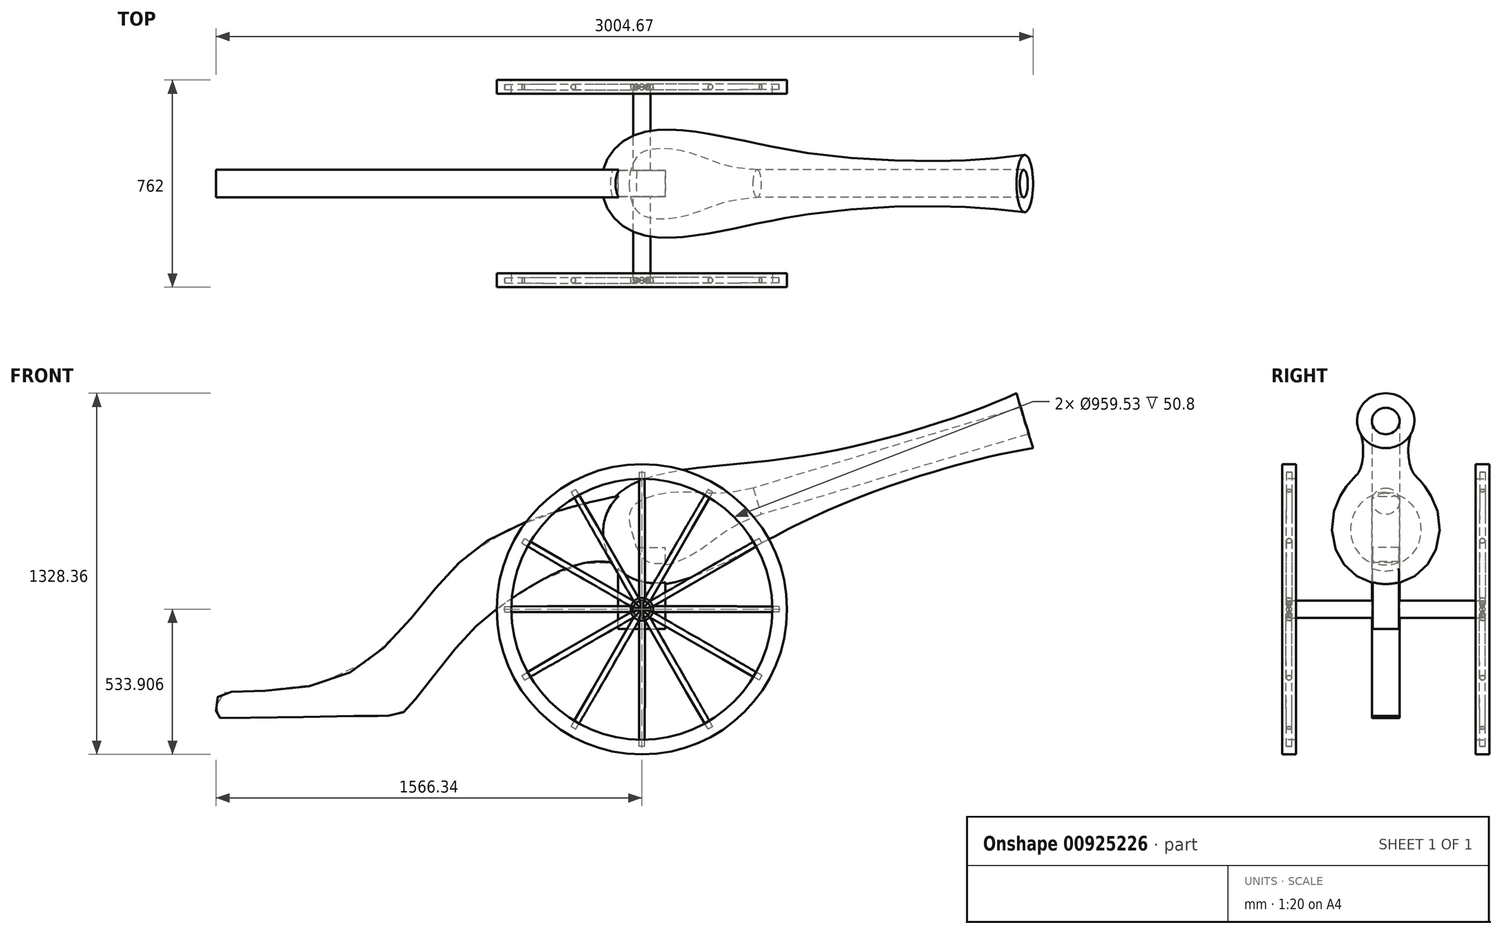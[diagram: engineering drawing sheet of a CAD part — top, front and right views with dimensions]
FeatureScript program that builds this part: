
annotation { "Feature Type Name" : "Feature", "Feature Type Description" : "" }
export const myFeature = defineFeature(function(context is Context, id is Id, definition is map)
    precondition{}
    {
        {
            var Q0;
            Q0=qCreatedBy(makeId("Front.planeOp"),FACE);
            var sketch = newSketch(context, id + "F0", { "sketchPlane" : qUnion([Q0])});
            skLineSegment(sketch, "E0", {"start": v(0, 0) * mm, "end": v(109.65, 33) * mm});
            skFitSpline(sketch, "E1", {"points": [v(0, 0) * mm, v(72.99, 213.2) * mm, v(629.9, 321.57) * mm, v(1200.16, 448.3) * mm, v(1516.96, 566.68) * mm], "startDerivative": vector(-414.8, 1258.42) * mm, "endDerivative": vector(1249.5, 571.91) * mm});
            skLineSegment(sketch, "E2", {"start": v(1516.96, 566.68) * mm, "end": v(1528.95, 513.26) * mm});
            skLineSegment(sketch, "E3", {"start": v(1528.95, 513.26) * mm, "end": v(548.63, 218.19) * mm});
            skFitSpline(sketch, "E4", {"points": [v(548.63, 218.19) * mm, v(418.02, 198.46) * mm, v(244.4, 200.95) * mm, v(100.74, 141) * mm, v(109.65, 33) * mm], "startDerivative": vector(-524.4, -115.88) * mm, "endDerivative": vector(178.23, -541.47) * mm});
            skSolve(sketch);
        }
        {
            var Q0;
            Q0 = qSketchRegion(id + "F0", true);
            var Q1;
            Q1=sQuery(id+"F0.wireOp",EDGE,"E0");
            revolve(context, id + "F1", {"surfaceOperationType" : NewSurfaceOperationType.NEW, "entities" : qUnion([Q0]), "axis" : qUnion([Q1]), "revolveType" : RevolveType.FULL});
        }
        {
            var Q0;
            Q0=qCreatedBy(makeId("Top.planeOp"),FACE);
            var sketch = newSketch(context, id + "F2", { "sketchPlane" : qUnion([Q0])});
            skLineSegment(sketch, "E5.bottom", {"start": v(51.83, 48.12) * mm, "end": v(225.99, 48.12) * mm});
            skLineSegment(sketch, "E5.top", {"start": v(51.83, -48.12) * mm, "end": v(225.99, -48.12) * mm});
            skLineSegment(sketch, "E5.left", {"start": v(51.83, 48.12) * mm, "end": v(51.83, -48.12) * mm});
            skLineSegment(sketch, "E5.right", {"start": v(225.99, 48.12) * mm, "end": v(225.99, -48.12) * mm});
            skPoint(sketch, "E5.middle", {"position": v(138.9, 0) * mm});
            skSolve(sketch);
        }
        {
            var Q0;
            Q0 = qSketchRegion(id + "F2", true);
            extrude(context, id + "F3", {"entities" : qUnion([Q0]), "operationType" : NewBodyOperationType.ADD, "oppositeDirection" : true, "depth" : 299.72 * mm, "offsetDistance" : 25.4 * mm});
        }
        {
            var Q0;
            Q0=qCreatedBy(makeId("Front.planeOp"),FACE);
            var sketch = newSketch(context, id + "F4", { "sketchPlane" : qUnion([Q0])});
            skFitSpline(sketch, "E6", {"points": [v(98.81, 191.9) * mm, v(-314.4, 82.48) * mm, v(-634.52, -169.04) * mm, v(-995.47, -487.53) * mm, v(-1402.16, -536.53) * mm, v(-1423.39, -561.03) * mm, v(-1425.02, -619.82) * mm, v(-1393.99, -627.99) * mm, v(-840.31, -619.82) * mm, v(-825.61, -619.82) * mm, v(-757.02, -614.92) * mm, v(-708.02, -577.36) * mm, v(-521.83, -343.8) * mm, v(-345.44, -191.9) * mm, v(-53.08, -54.71) * mm, v(59.61, -53.08) * mm, v(59.61, -36.75) * mm, v(30.22, 28.58) * mm, v(59.61, 157.6) * mm, v(98.81, 191.9) * mm]});
            skSolve(sketch);
        }
        {
            var Q0;
            Q0 = qSketchRegion(id + "F4", true);
            extrude(context, id + "F5", {"entities" : qUnion([Q0]), "operationType" : NewBodyOperationType.ADD, "depth" : 50.8 * mm, "offsetDistance" : 25.4 * mm, "hasSecondDirection" : true, "secondDirectionOppositeDirection" : true, "secondDirectionDepth" : 50.8 * mm});
        }
        {
            var Q0;
            Q0=qCreatedBy(makeId("Front.planeOp"),FACE);
            var sketch = newSketch(context, id + "F6", { "sketchPlane" : qUnion([Q0])});
            skLineSegment(sketch, "E7", {"start": v(139.4, -303.65) * mm, "end": v(139.4, -227.77) * mm});
            skCircle(sketch, "E8", {"center": v(139.4, -227.77) * mm, "radius": 31.75 * mm});
            skSolve(sketch);
        }
        {
            var Q0;
            Q0 = qSketchRegion(id + "F6", true);
            extrude(context, id + "F7", {"entities" : qUnion([Q0]), "operationType" : NewBodyOperationType.ADD, "depth" : 355.6 * mm, "offsetDistance" : 25.4 * mm, "hasSecondDirection" : true, "secondDirectionOppositeDirection" : true, "secondDirectionDepth" : 355.6 * mm});
        }
        {
            var Q0;
            Q0=makeQuery(id+"F7.opExtrude","CAP_FACE",FACE,{"disambiguationData":[OSD([sQuery(id+"F6.wireOp",EDGE,"E8")])],"isStart":false});
            var sketch = newSketch(context, id + "F8", { "sketchPlane" : qUnion([Q0])});
            skCircle(sketch, "E9", {"center": v(139.4, -227.77) * mm, "radius": 533.9 * mm});
            skCircle(sketch, "E10", {"center": v(139.4, -227.77) * mm, "radius": 479.77 * mm});
            skSolve(sketch);
        }
        {
            var Q0;
            Q0 = qSketchRegion(id + "F8", true);
            extrude(context, id + "F9", {"entities" : qUnion([Q0]), "oppositeDirection" : true, "depth" : 25.4 * mm, "offsetDistance" : 25.4 * mm, "hasSecondDirection" : true, "secondDirectionOppositeDirection" : false, "secondDirectionDepth" : 25.4 * mm});
        }
        {
            var Q0;
            Q0=makeQuery(id+"F7.opExtrude","CAP_FACE",FACE,{"disambiguationData":[OSD([sQuery(id+"F6.wireOp",EDGE,"E8")])],"isStart":false});
            var sketch = newSketch(context, id + "F10", { "sketchPlane" : qUnion([Q0])});
            skLineSegment(sketch, "E11", {"start": v(139.4, -227.77) * mm, "end": v(139.4, -731.61) * mm});
            skLineSegment(sketch, "E12", {"start": v(139.4, -731.61) * mm, "end": v(149.15, -731.61) * mm});
            skLineSegment(sketch, "E13", {"start": v(149.15, -731.61) * mm, "end": v(150.2, -575.12) * mm});
            skLineSegment(sketch, "E14", {"start": v(150.2, -575.12) * mm, "end": v(150.2, -269.13) * mm});
            skLineSegment(sketch, "E15", {"start": v(150.2, -269.13) * mm, "end": v(139.4, -227.77) * mm});
            skSolve(sketch);
        }
        {
            var Q0;
            Q0 = qSketchRegion(id + "F10", true);
            var Q1;
            Q1=sQuery(id+"F10.wireOp",EDGE,"E11");
            revolve(context, id + "F11", {"surfaceOperationType" : NewSurfaceOperationType.NEW, "entities" : qUnion([Q0]), "axis" : qUnion([Q1]), "revolveType" : RevolveType.FULL});
        }
        {
            var Q0;
            Q0=makeQuery(id+"F11.opRevolve","SWEPT_BODY",BODY,{"disambiguationData":[OSD([sQuery(id+"F10.wireOp",EDGE,"E11"),sQuery(id+"F10.wireOp",EDGE,"E12"),sQuery(id+"F10.wireOp",EDGE,"E13"),sQuery(id+"F10.wireOp",EDGE,"E14"),sQuery(id+"F10.wireOp",EDGE,"E15")])]});
            var Q1;
            Q1=makeQuery(id+"F7.opExtrude","CAP_EDGE",EDGE,{"disambiguationData":[OSD([sQuery(id+"F6.wireOp",EDGE,"E8")])],"isStart":false});
            circularPattern(context, id + "F12", {"entities" : qUnion([Q0]), "axis" : qUnion([Q1]), "angle" : 360 * degree, "instanceCount" : 12, "equalSpace" : true});
        }
        {
            var Q0;
            Q0=makeQuery(id+"F9.opExtrude","SWEPT_BODY",BODY,{"disambiguationData":[OSD([sQuery(id+"F8.wireOp",EDGE,"E9"),sQuery(id+"F8.wireOp",EDGE,"E10")])]});
            var Q1;
            Q1=makeQuery(id+"F12.opPattern","COPY",BODY,{"derivedFrom":makeQuery(id+"F11.opRevolve","SWEPT_BODY",BODY,{"disambiguationData":[OSD([sQuery(id+"F10.wireOp",EDGE,"E11"),sQuery(id+"F10.wireOp",EDGE,"E12"),sQuery(id+"F10.wireOp",EDGE,"E13"),sQuery(id+"F10.wireOp",EDGE,"E14"),sQuery(id+"F10.wireOp",EDGE,"E15")])]}),"instanceName":"4"});
            var Q2;
            Q2=makeQuery(id+"F12.opPattern","COPY",BODY,{"derivedFrom":makeQuery(id+"F11.opRevolve","SWEPT_BODY",BODY,{"disambiguationData":[OSD([sQuery(id+"F10.wireOp",EDGE,"E11"),sQuery(id+"F10.wireOp",EDGE,"E12"),sQuery(id+"F10.wireOp",EDGE,"E13"),sQuery(id+"F10.wireOp",EDGE,"E14"),sQuery(id+"F10.wireOp",EDGE,"E15")])]}),"instanceName":"3"});
            var Q3;
            Q3=makeQuery(id+"F12.opPattern","COPY",BODY,{"derivedFrom":makeQuery(id+"F11.opRevolve","SWEPT_BODY",BODY,{"disambiguationData":[OSD([sQuery(id+"F10.wireOp",EDGE,"E11"),sQuery(id+"F10.wireOp",EDGE,"E12"),sQuery(id+"F10.wireOp",EDGE,"E13"),sQuery(id+"F10.wireOp",EDGE,"E14"),sQuery(id+"F10.wireOp",EDGE,"E15")])]}),"instanceName":"2"});
            var Q4;
            Q4=makeQuery(id+"F12.opPattern","COPY",BODY,{"derivedFrom":makeQuery(id+"F11.opRevolve","SWEPT_BODY",BODY,{"disambiguationData":[OSD([sQuery(id+"F10.wireOp",EDGE,"E11"),sQuery(id+"F10.wireOp",EDGE,"E12"),sQuery(id+"F10.wireOp",EDGE,"E13"),sQuery(id+"F10.wireOp",EDGE,"E14"),sQuery(id+"F10.wireOp",EDGE,"E15")])]}),"instanceName":"1"});
            var Q5;
            Q5=makeQuery(id+"F11.opRevolve","SWEPT_BODY",BODY,{"disambiguationData":[OSD([sQuery(id+"F10.wireOp",EDGE,"E11"),sQuery(id+"F10.wireOp",EDGE,"E12"),sQuery(id+"F10.wireOp",EDGE,"E13"),sQuery(id+"F10.wireOp",EDGE,"E14"),sQuery(id+"F10.wireOp",EDGE,"E15")])]});
            var Q6;
            Q6=makeQuery(id+"F12.opPattern","COPY",BODY,{"derivedFrom":makeQuery(id+"F11.opRevolve","SWEPT_BODY",BODY,{"disambiguationData":[OSD([sQuery(id+"F10.wireOp",EDGE,"E11"),sQuery(id+"F10.wireOp",EDGE,"E12"),sQuery(id+"F10.wireOp",EDGE,"E13"),sQuery(id+"F10.wireOp",EDGE,"E14"),sQuery(id+"F10.wireOp",EDGE,"E15")])]}),"instanceName":"11"});
            var Q7;
            Q7=makeQuery(id+"F12.opPattern","COPY",BODY,{"derivedFrom":makeQuery(id+"F11.opRevolve","SWEPT_BODY",BODY,{"disambiguationData":[OSD([sQuery(id+"F10.wireOp",EDGE,"E11"),sQuery(id+"F10.wireOp",EDGE,"E12"),sQuery(id+"F10.wireOp",EDGE,"E13"),sQuery(id+"F10.wireOp",EDGE,"E14"),sQuery(id+"F10.wireOp",EDGE,"E15")])]}),"instanceName":"10"});
            var Q8;
            Q8=makeQuery(id+"F12.opPattern","COPY",BODY,{"derivedFrom":makeQuery(id+"F11.opRevolve","SWEPT_BODY",BODY,{"disambiguationData":[OSD([sQuery(id+"F10.wireOp",EDGE,"E11"),sQuery(id+"F10.wireOp",EDGE,"E12"),sQuery(id+"F10.wireOp",EDGE,"E13"),sQuery(id+"F10.wireOp",EDGE,"E14"),sQuery(id+"F10.wireOp",EDGE,"E15")])]}),"instanceName":"9"});
            var Q9;
            Q9=makeQuery(id+"F12.opPattern","COPY",BODY,{"derivedFrom":makeQuery(id+"F11.opRevolve","SWEPT_BODY",BODY,{"disambiguationData":[OSD([sQuery(id+"F10.wireOp",EDGE,"E11"),sQuery(id+"F10.wireOp",EDGE,"E12"),sQuery(id+"F10.wireOp",EDGE,"E13"),sQuery(id+"F10.wireOp",EDGE,"E14"),sQuery(id+"F10.wireOp",EDGE,"E15")])]}),"instanceName":"8"});
            var Q10;
            Q10=makeQuery(id+"F12.opPattern","COPY",BODY,{"derivedFrom":makeQuery(id+"F11.opRevolve","SWEPT_BODY",BODY,{"disambiguationData":[OSD([sQuery(id+"F10.wireOp",EDGE,"E11"),sQuery(id+"F10.wireOp",EDGE,"E12"),sQuery(id+"F10.wireOp",EDGE,"E13"),sQuery(id+"F10.wireOp",EDGE,"E14"),sQuery(id+"F10.wireOp",EDGE,"E15")])]}),"instanceName":"7"});
            var Q11;
            Q11=makeQuery(id+"F12.opPattern","COPY",BODY,{"derivedFrom":makeQuery(id+"F11.opRevolve","SWEPT_BODY",BODY,{"disambiguationData":[OSD([sQuery(id+"F10.wireOp",EDGE,"E11"),sQuery(id+"F10.wireOp",EDGE,"E12"),sQuery(id+"F10.wireOp",EDGE,"E13"),sQuery(id+"F10.wireOp",EDGE,"E14"),sQuery(id+"F10.wireOp",EDGE,"E15")])]}),"instanceName":"6"});
            var Q12;
            Q12=makeQuery(id+"F12.opPattern","COPY",BODY,{"derivedFrom":makeQuery(id+"F11.opRevolve","SWEPT_BODY",BODY,{"disambiguationData":[OSD([sQuery(id+"F10.wireOp",EDGE,"E11"),sQuery(id+"F10.wireOp",EDGE,"E12"),sQuery(id+"F10.wireOp",EDGE,"E13"),sQuery(id+"F10.wireOp",EDGE,"E14"),sQuery(id+"F10.wireOp",EDGE,"E15")])]}),"instanceName":"5"});
            var Q13;
            Q13=qCreatedBy(makeId("Front.planeOp"),FACE);
            mirror(context, id + "F13", {"entities" : qUnion([Q0, Q1, Q2, Q3, Q4, Q5, Q6, Q7, Q8, Q9, Q10, Q11, Q12]), "mirrorPlane" : qUnion([Q13])});
        }
    });
